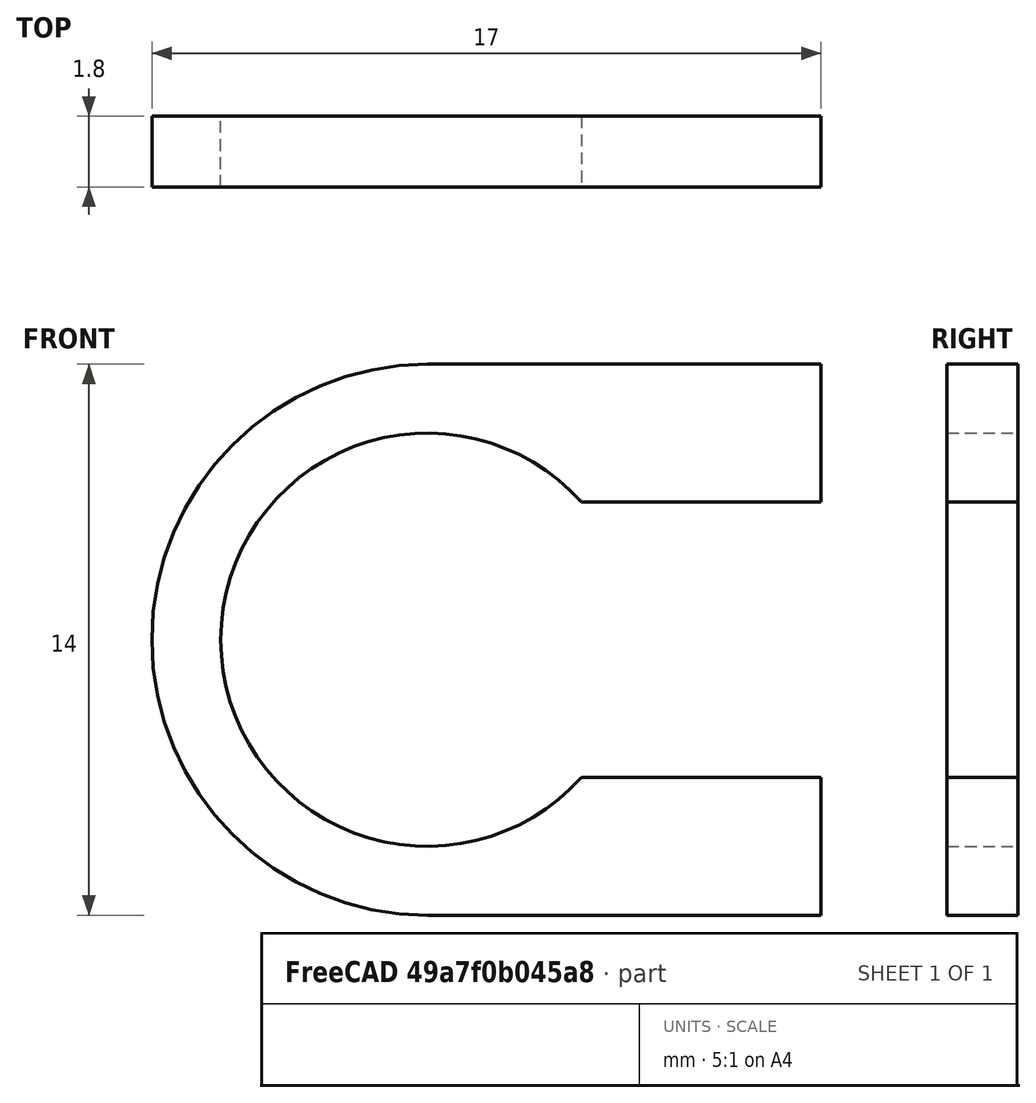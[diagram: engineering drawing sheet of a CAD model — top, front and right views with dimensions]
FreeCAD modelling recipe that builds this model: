
FCSTD DOCUMENT  (FreeCAD 0.21R33668 +26 (Git))
Label: Cover_Gear
License: All rights reserved
LicenseURL: https://en.wikipedia.org/wiki/All_rights_reserved
objects: Sketcher::SketchObject×1, PartDesign::Pad×1, PartDesign::Body×1
note: 4 computed .brp shape members not serialized (recipe doc carries the construction recipe); baked Part::Feature solids carry a one-line shape summary decoded from their .brp

FEATURE [Sketcher::SketchObject] Sketch
  FullyConstrained = true
  MapMode = 5
  Placement = pos=(0,0,0) rot=(1,0,0;1.5708rad)
  Support = -> [XZ_Plane]
  sketch-geometry (8):
    g0: ArcOfCircle CenterX=0 CenterY=0 CenterZ=0 NormalX=0 NormalY=0 NormalZ=1 AngleXU=0 Radius=5.25 StartAngle=0.730618 EndAngle=5.55257
    g1: ArcOfCircle CenterX=0 CenterY=0 CenterZ=0 NormalX=0 NormalY=0 NormalZ=1 AngleXU=0 Radius=7 StartAngle=1.5708 EndAngle=4.71239
    g2: LineSegment StartX=3.91 StartY=3.50348 StartZ=0 EndX=10 EndY=3.50348 EndZ=0
    g3: LineSegment StartX=10 StartY=-3.50348 StartZ=0 EndX=3.91 EndY=-3.50348 EndZ=0
    g4: LineSegment StartX=-1.1e-15 StartY=7 StartZ=0 EndX=10 EndY=7 EndZ=0
    g5: LineSegment StartX=10 StartY=7 StartZ=0 EndX=10 EndY=3.50348 EndZ=0
    g6: LineSegment StartX=10 StartY=-7 StartZ=0 EndX=-1.8e-15 EndY=-7 EndZ=0
    g7: LineSegment StartX=10 StartY=-3.50348 StartZ=0 EndX=10 EndY=-7 EndZ=0
  constraints (22):
    c: Coincident(g0,g-1)
    c: Diameter(g0) = 10.5
    c: Coincident(g1,g0)
    c: Diameter(g1) = 14
    c: Horizontal(g2)
    c: Horizontal(g3)
    c: Coincident(g4,g5)
    c: Coincident(g7,g6)
    c: Horizontal(g4)
    c: Horizontal(g6)
    c: Vertical(g5)
    c: DistanceX(g0,g4) = 10
    c: Coincident(g0,g3)
    c: Coincident(g0,g2)
    c: Tangent(g1,g4) = 1.5708
    c: Tangent(g1,g6) = 1.5708
    c: Vertical(g0,g0)
    c: DistanceX(g2,g2) = 6.09
    c: Coincident(g5,g2)
    c: Coincident(g7,g3)
    c: Vertical(g2,g3)
    c: Vertical(g7)
FEATURE [PartDesign::Pad] Pad
  Direction = (0,-1,2e-16)
  Length = 1.8
  Length2 = 10
  Placement = pos=(0,0,0) rot=(1,0,0;1.5708rad)
  Profile = -> Sketch
  ReferenceAxis = -> Sketch [N_Axis]
  Type = 0
FEATURE [PartDesign::Body] Body
  Group = -> [Sketch,Pad]
  Origin = -> Origin
  Tip = -> Pad
